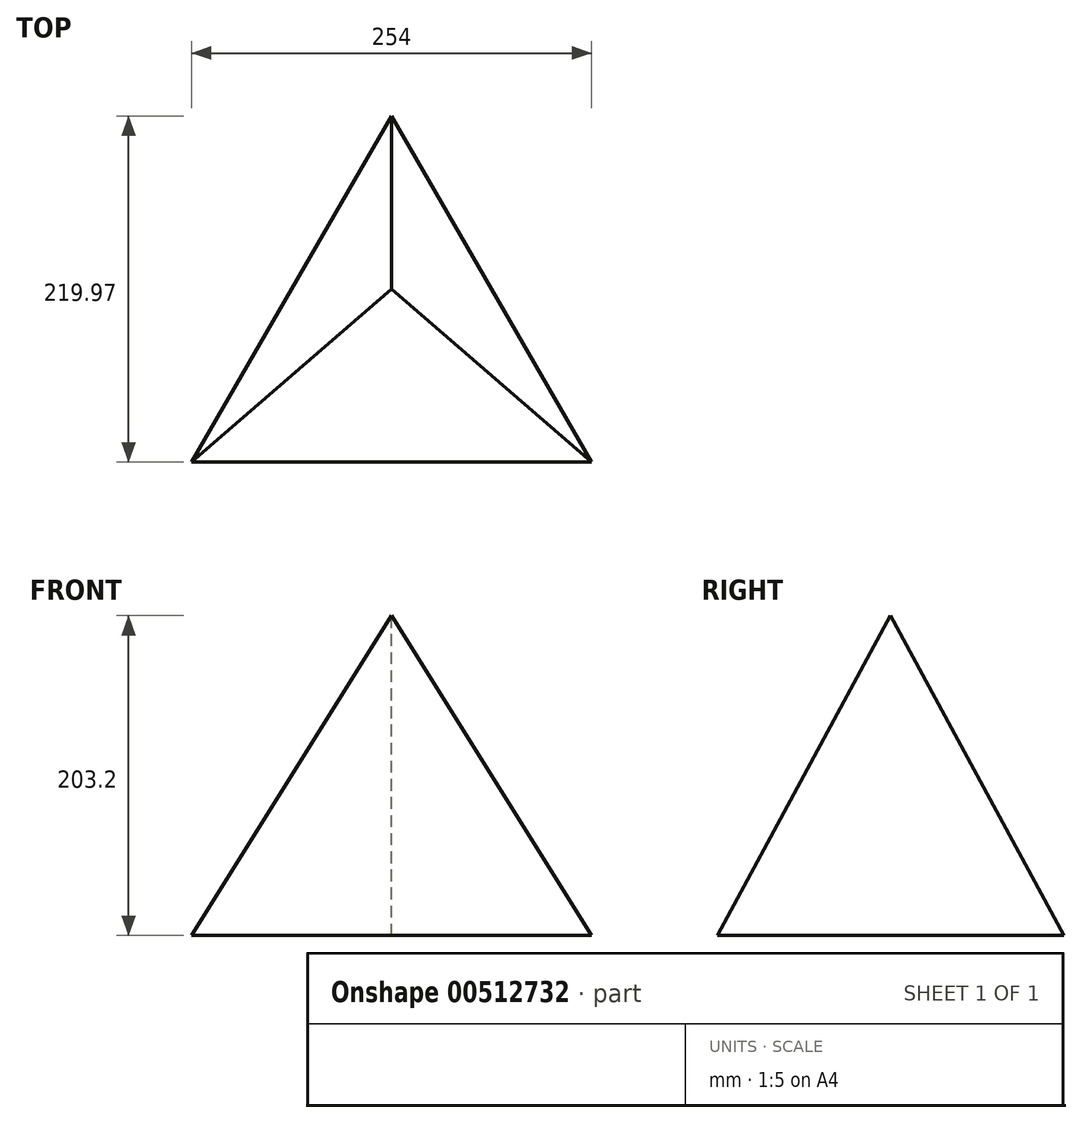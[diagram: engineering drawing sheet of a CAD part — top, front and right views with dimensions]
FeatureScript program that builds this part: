
annotation { "Feature Type Name" : "Feature", "Feature Type Description" : "" }
export const myFeature = defineFeature(function(context is Context, id is Id, definition is map)
    precondition{}
    {
        {
            var Q0;
            Q0=qCreatedBy(makeId("Top.planeOp"),FACE);
            var sketch = newSketch(context, id + "F0", { "sketchPlane" : qUnion([Q0])});
            skLineSegment(sketch, "E0", {"start": v(-127, -114.26) * mm, "end": v(0, 105.7) * mm});
            skLineSegment(sketch, "E1", {"start": v(0, 105.7) * mm, "end": v(127, -114.26) * mm});
            skLineSegment(sketch, "E2", {"start": v(127, -114.26) * mm, "end": v(-127, -114.26) * mm});
            skSolve(sketch);
        }
        {
            var Q0;
            Q0=qCreatedBy(makeId("Top.planeOp"),FACE);
            cPlane(context, id + "F1", {"entities" : qUnion([Q0]), "cplaneType" : CPlaneType.OFFSET, "offset" : 203.2 * mm, "width" : 152.4 * mm, "height" : 152.4 * mm});
        }
        {
            var Q0;
            Q0=qCreatedBy(id+"F1.planeOp",FACE);
            var sketch = newSketch(context, id + "F2", { "sketchPlane" : qUnion([Q0])});
            skPoint(sketch, "E3", {"position": v(0, -4.28) * mm});
            skPoint(sketch, "E4.0", {"position": v(0, 105.7) * mm});
            skPoint(sketch, "E5.0", {"position": v(0, -114.26) * mm});
            skSolve(sketch);
        }
        {
            var Q0;
            Q0=makeQuery(id+"F0.imprint","IMPRINT",FACE,{"disambiguationData":[TD([[makeQuery(id+"F0.imprint","IMPRINT",EDGE,{"derivedFrom":sQuery(id+"F0.wireOp",EDGE,"E0")}),-1.0]])]});
            var Q1;
            Q1=sQuery(id+"F2.wireOp",VERTEX,"E3");
            loft(context, id + "F3", {"sheetProfilesArray" : [{ "sheetProfileEntities" : qUnion([Q0]) }, { "sheetProfileEntities" : qUnion([Q1]) }]});
        }
    });
